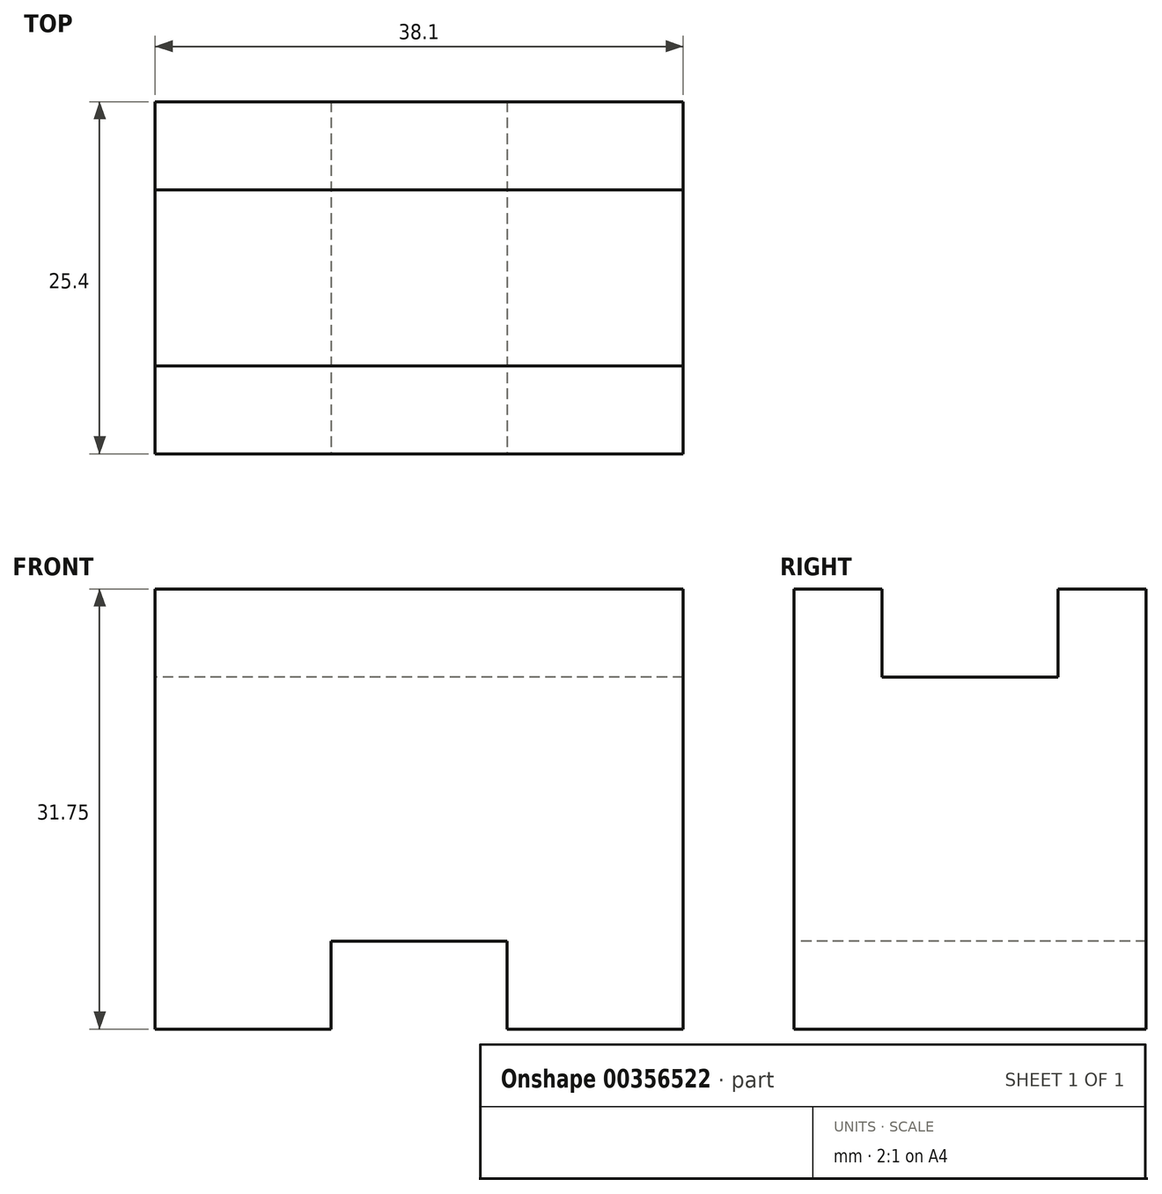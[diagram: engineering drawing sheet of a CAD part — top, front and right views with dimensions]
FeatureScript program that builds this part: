
annotation { "Feature Type Name" : "Feature", "Feature Type Description" : "" }
export const myFeature = defineFeature(function(context is Context, id is Id, definition is map)
    precondition{}
    {
        {
            var Q0;
            Q0=qCreatedBy(makeId("Right.planeOp"),FACE);
            var sketch = newSketch(context, id + "F0", { "sketchPlane" : qUnion([Q0])});
            skLineSegment(sketch, "E0", {"start": v(0, 0) * mm, "end": v(0, 31.75) * mm});
            skLineSegment(sketch, "E1", {"start": v(0, 31.75) * mm, "end": v(6.35, 31.75) * mm});
            skLineSegment(sketch, "E2", {"start": v(6.35, 31.75) * mm, "end": v(6.35, 25.4) * mm});
            skLineSegment(sketch, "E3", {"start": v(6.35, 25.4) * mm, "end": v(19.05, 25.4) * mm});
            skLineSegment(sketch, "E4", {"start": v(19.05, 25.4) * mm, "end": v(19.05, 31.75) * mm});
            skLineSegment(sketch, "E5", {"start": v(19.05, 31.75) * mm, "end": v(25.4, 31.75) * mm});
            skLineSegment(sketch, "E6", {"start": v(25.4, 31.75) * mm, "end": v(25.4, 0) * mm});
            skLineSegment(sketch, "E7", {"start": v(25.4, 0) * mm, "end": v(0, 0) * mm});
            skSolve(sketch);
        }
        {
            var Q0;
            Q0 = qSketchRegion(id + "F0", true);
            extrude(context, id + "F1", {"entities" : qUnion([Q0]), "depth" : 38.1 * mm});
        }
        {
            var Q0;
            Q0=qCreatedBy(makeId("Front.planeOp"),FACE);
            var sketch = newSketch(context, id + "F2", { "sketchPlane" : qUnion([Q0])});
            skLineSegment(sketch, "E8", {"start": v(0, 0) * mm, "end": v(12.7, 0) * mm});
            skLineSegment(sketch, "E9", {"start": v(12.7, 0) * mm, "end": v(12.7, 6.35) * mm});
            skLineSegment(sketch, "E10", {"start": v(12.7, 6.35) * mm, "end": v(25.4, 6.35) * mm});
            skLineSegment(sketch, "E11", {"start": v(25.4, 6.35) * mm, "end": v(25.4, 0) * mm});
            skLineSegment(sketch, "E12", {"start": v(25.4, 0) * mm, "end": v(38.1, 0) * mm});
            skLineSegment(sketch, "E13", {"start": v(12.7, 0) * mm, "end": v(25.4, 0) * mm});
            skSolve(sketch);
        }
        {
            var Q0;
            Q0 = qSketchRegion(id + "F2", true);
            extrude(context, id + "F3", {"entities" : qUnion([Q0]), "operationType" : NewBodyOperationType.REMOVE, "oppositeDirection" : true, "depth" : 31.75 * mm});
        }
    });
